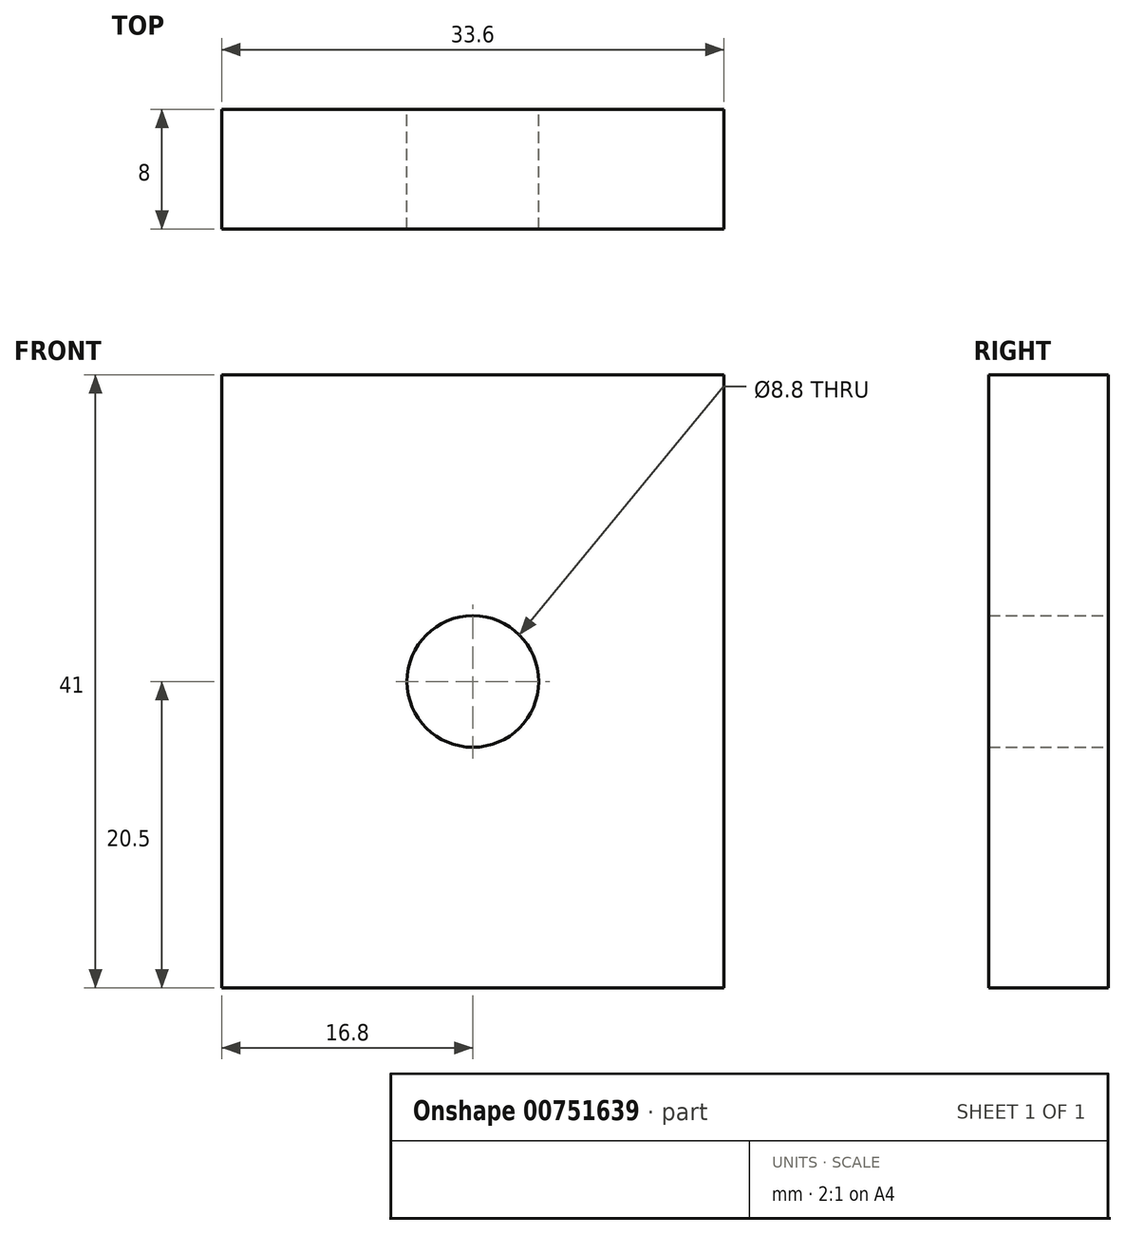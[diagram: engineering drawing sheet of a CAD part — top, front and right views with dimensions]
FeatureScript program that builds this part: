
annotation { "Feature Type Name" : "Feature", "Feature Type Description" : "" }
export const myFeature = defineFeature(function(context is Context, id is Id, definition is map)
    precondition{}
    {
        {
            var Q0;
            Q0=qCreatedBy(makeId("Top.planeOp"),FACE);
            var sketch = newSketch(context, id + "F0", { "sketchPlane" : qUnion([Q0])});
            skLineSegment(sketch, "E0.bottom", {"start": v(0, 0) * mm, "end": v(33.6, 0) * mm});
            skLineSegment(sketch, "E0.top", {"start": v(0, 8) * mm, "end": v(33.6, 8) * mm});
            skLineSegment(sketch, "E0.left", {"start": v(0, 0) * mm, "end": v(0, 8) * mm});
            skLineSegment(sketch, "E0.right", {"start": v(33.6, 0) * mm, "end": v(33.6, 8) * mm});
            skSolve(sketch);
        }
        {
            var Q0;
            Q0=qSketchRegion(id+"F0",true);
            extrude(context, id + "F1", {"entities" : qUnion([Q0]), "depth" : 41 * mm});
        }
        {
            var Q0;
            Q0=makeQuery(id+"F1.opExtrude","SWEPT_FACE",FACE,{"disambiguationData":[OSD([sQuery(id+"F0.wireOp",EDGE,"E0.top")])]});
            var sketch = newSketch(context, id + "F2", { "sketchPlane" : qUnion([Q0])});
            skCircle(sketch, "E1", {"center": v(-16.8, 20.5) * mm, "radius": 3.08 * mm});
            skPoint(sketch, "E1.centerSnap0", {"position": v(-16.8, 0) * mm});
            skPoint(sketch, "E1.centerSnap1", {"position": v(-33.6, 20.5) * mm});
            skSolve(sketch);
        }
        {
            var Q0;
            Q0=sQuery(id+"F2.wireOp",VERTEX,"E1.center");
            var Q1;
            Q1=makeQuery(id+"F1.opExtrude","SWEPT_BODY",BODY,{"disambiguationData":[OSD([sQuery(id+"F0.wireOp",EDGE,"E0.bottom"),sQuery(id+"F0.wireOp",EDGE,"E0.top"),sQuery(id+"F0.wireOp",EDGE,"E0.left"),sQuery(id+"F0.wireOp",EDGE,"E0.right")])]});
            hole(context, id + "F3", {"style" : HoleStyle.SIMPLE, "endStyle" : HoleEndStyle.THROUGH, "standardTappedOrClearance" : lookupTablePath({ "standard" : "ISO", "engagement" : "75%", "pitch" : "1.25 mm", "size" : "M10", "type" : "Tapped" }), "standardBlindInLast" : lookupTablePath({ "standard" : "ISO", "engagement" : "75%", "pitch" : "1.25 mm", "size" : "M10", "type" : "Tapped" }), "holeDiameter" : 8.8 * mm, "locations" : qUnion([Q0]), "scope" : qUnion([Q1]), "isTappedThrough" : true, "majorDiameter" : 10 * mm, "showTappedDepth" : true});
        }
    });
